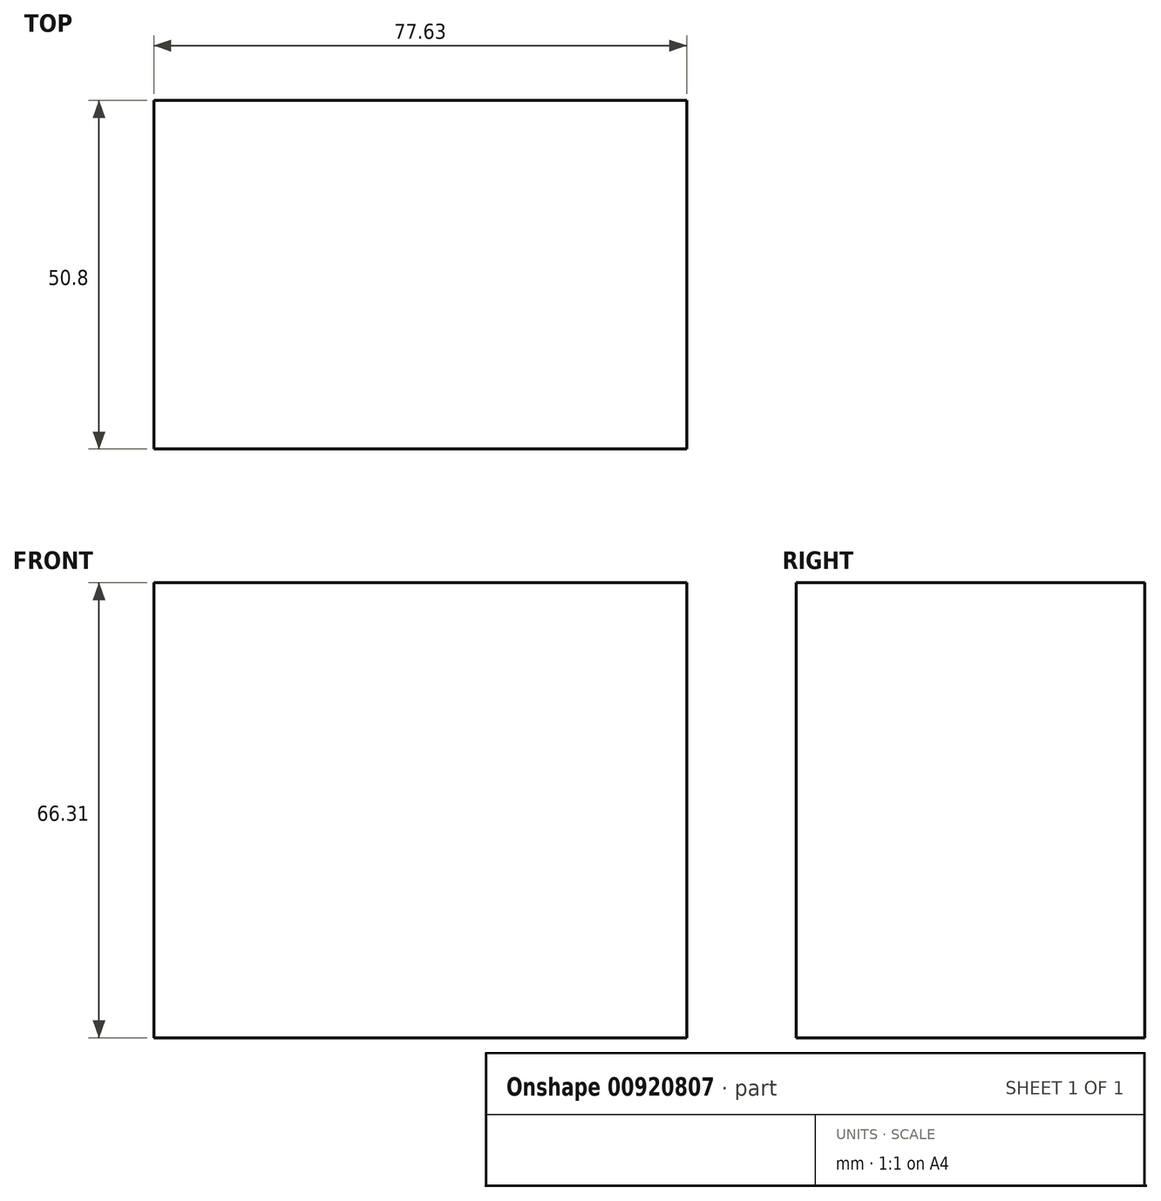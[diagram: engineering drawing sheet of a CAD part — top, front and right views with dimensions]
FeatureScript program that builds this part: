
annotation { "Feature Type Name" : "Feature", "Feature Type Description" : "" }
export const myFeature = defineFeature(function(context is Context, id is Id, definition is map)
    precondition{}
    {
        {
            var Q0;
            Q0=qCreatedBy(makeId("Front.planeOp"),FACE);
            var sketch = newSketch(context, id + "F0", { "sketchPlane" : qUnion([Q0])});
            skLineSegment(sketch, "E0.bottom", {"start": v(-44.1, 42.98) * mm, "end": v(33.53, 42.98) * mm});
            skLineSegment(sketch, "E0.top", {"start": v(-44.1, -23.33) * mm, "end": v(33.53, -23.33) * mm});
            skLineSegment(sketch, "E0.left", {"start": v(-44.1, 42.98) * mm, "end": v(-44.1, -23.33) * mm});
            skLineSegment(sketch, "E0.right", {"start": v(33.53, 42.98) * mm, "end": v(33.53, -23.33) * mm});
            skSolve(sketch);
        }
        {
            var Q0;
            Q0=makeQuery(id+"F0.imprint","IMPRINT",FACE,{"disambiguationData":[TD([[makeQuery(id+"F0.imprint","IMPRINT",EDGE,{"derivedFrom":sQuery(id+"F0.wireOp",EDGE,"E0.bottom")}),-1.0]])]});
            extrude(context, id + "F1", {"entities" : qUnion([Q0]), "depth" : 25.4 * mm, "offsetDistance" : 25.4 * mm, "hasSecondDirection" : true, "secondDirectionOppositeDirection" : true, "secondDirectionDepth" : 25.4 * mm});
        }
    });
